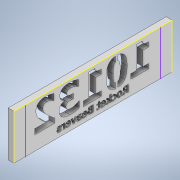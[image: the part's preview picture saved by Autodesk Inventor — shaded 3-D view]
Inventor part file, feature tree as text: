
AUTODESK INVENTOR PART (.ipt)
format: ipt  version: 2020 (Build 240168000, 168)  size: 702,464 bytes
history: native  units: in
note: dims shown in document units (in); Inventor stores cm internally (conversion verified against a paired STEP export)
features: sketch x5, extrude x3, emboss x1
ambient origin geometry x8: Origin, YZ Plane, XZ Plane, XY Plane, X Axis, Y Axis, Z Axis, Center Point
bodies: Solid1 (feature_tree)
feature tree (9):
  extrude  "Extrusion1"  Depth=7.0in
  emboss  "Emboss1"
  extrude  "Extrusion2"  Depth=0.25in TaperAngle=0.0deg
  extrude  "Extrusion3"  Depth=0.1in
  sketch  "Sketch6"  dims[d10=0.01in d11=0.02in d12=0.01in d13=0.02in d14=0.02in d15=0.01in d16=0.02in d17=0.01in d18=0.01in d19=0.01in d20=0.01in d21=0.01in d22=0.01in d23=0.25in d24=0.0in]
  sketch  "Sketch1"  dims[d0=2.0in d1=7.0in]
  sketch  "Sketch3"  dims[d2=0.25in d3=0.0in d4=0.25in d5=0.0in]
  sketch  "Sketch4"  dims[d6=0.05in d7=0.1in]
  sketch  "Sketch5"  dims[d8=0.25in d9=0.0in]
